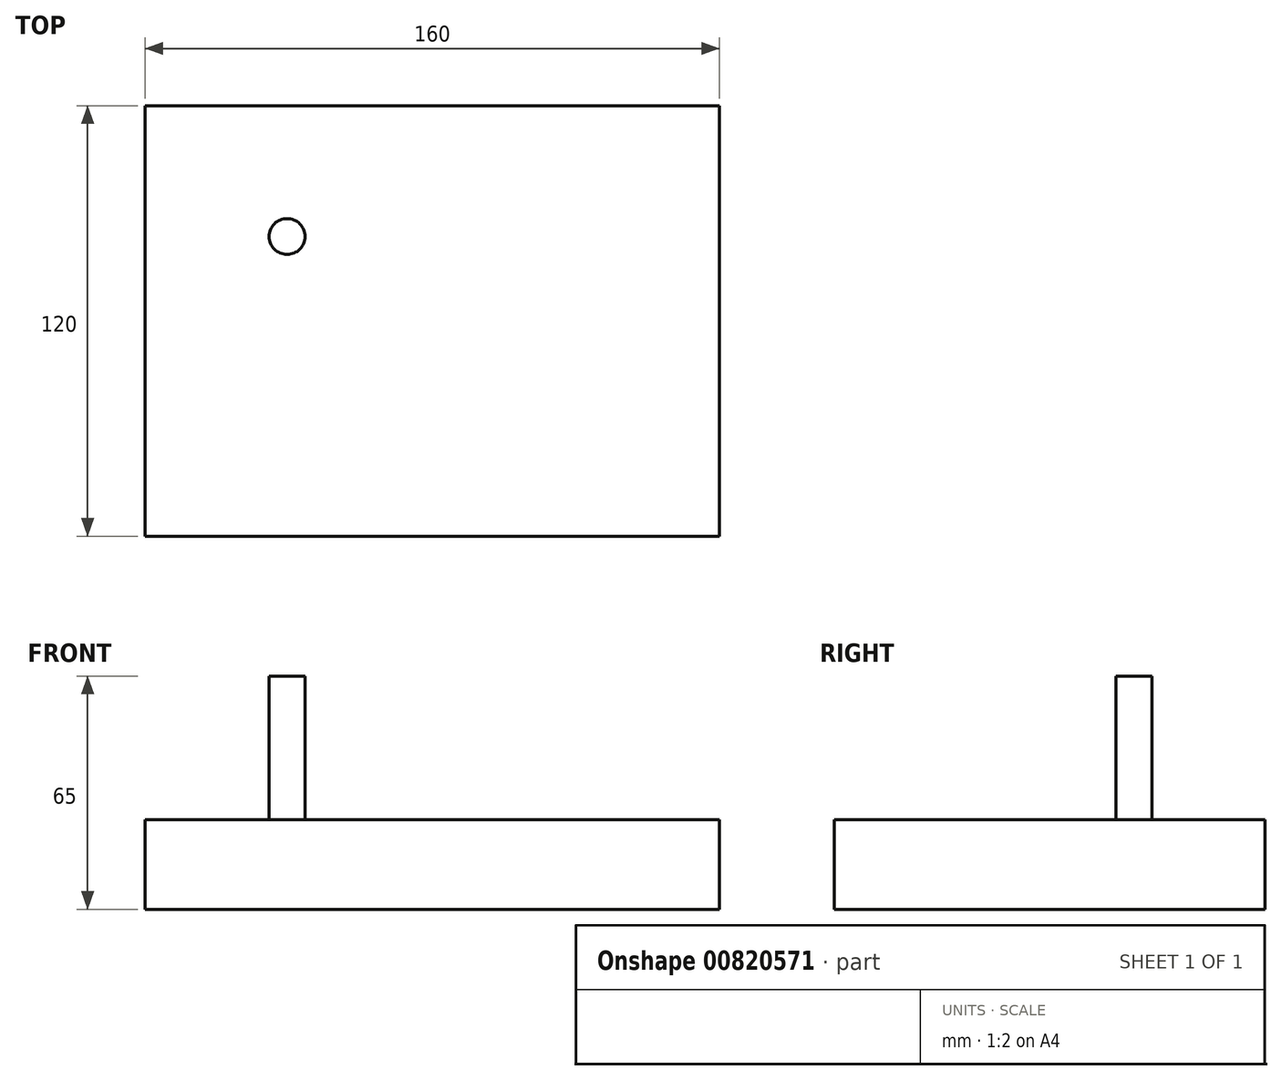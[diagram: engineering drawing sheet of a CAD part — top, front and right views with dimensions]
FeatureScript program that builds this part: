
annotation { "Feature Type Name" : "Feature", "Feature Type Description" : "" }
export const myFeature = defineFeature(function(context is Context, id is Id, definition is map)
    precondition{}
    {
        {
            var Q0;
            Q0=qCreatedBy(makeId("Top.planeOp"),FACE);
            var sketch = newSketch(context, id + "F0", { "sketchPlane" : qUnion([Q0])});
            skLineSegment(sketch, "E0.bottom", {"start": v(-115.2, 57.89) * mm, "end": v(44.8, 57.89) * mm});
            skLineSegment(sketch, "E0.top", {"start": v(-115.2, -62.11) * mm, "end": v(44.8, -62.11) * mm});
            skLineSegment(sketch, "E0.left", {"start": v(-115.2, 57.89) * mm, "end": v(-115.2, -62.11) * mm});
            skLineSegment(sketch, "E0.right", {"start": v(44.8, 57.89) * mm, "end": v(44.8, -62.11) * mm});
            skSolve(sketch);
        }
        {
            var Q0;
            Q0=makeQuery(id+"F0.imprint","IMPRINT",FACE,{"disambiguationData":[TD([[makeQuery(id+"F0.imprint","IMPRINT",EDGE,{"derivedFrom":sQuery(id+"F0.wireOp",EDGE,"E0.bottom")}),-1.0]])]});
            extrude(context, id + "F1", {"entities" : qUnion([Q0]), "depth" : 25 * mm, "offsetDistance" : 25 * mm});
        }
        {
            var Q0;
            Q0=makeQuery(id+"F1.opExtrude","CAP_FACE",FACE,{"disambiguationData":[OSD([sQuery(id+"F0.wireOp",EDGE,"E0.bottom"),sQuery(id+"F0.wireOp",EDGE,"E0.top"),sQuery(id+"F0.wireOp",EDGE,"E0.left"),sQuery(id+"F0.wireOp",EDGE,"E0.right")])],"isStart":false});
            var sketch = newSketch(context, id + "F2", { "sketchPlane" : qUnion([Q0])});
            skPoint(sketch, "E1", {"position": v(-75.65, 21.43) * mm});
            skCircle(sketch, "E2", {"center": v(-75.65, 21.43) * mm, "radius": 5 * mm});
            skSolve(sketch);
        }
        {
            var Q0;
            Q0=makeQuery(id+"F1.opExtrude","CAP_FACE",FACE,{"disambiguationData":[OSD([sQuery(id+"F0.wireOp",EDGE,"E0.bottom"),sQuery(id+"F0.wireOp",EDGE,"E0.top"),sQuery(id+"F0.wireOp",EDGE,"E0.left"),sQuery(id+"F0.wireOp",EDGE,"E0.right")])],"isStart":false});
            var sketch = newSketch(context, id + "F3", { "sketchPlane" : qUnion([Q0])});
            skCircle(sketch, "E3", {"center": v(-35.2, -2.11) * mm, "radius": 5.53 * mm});
            skSolve(sketch);
        }
        {
            var Q0;
            Q0=makeQuery(id+"F2.imprint","IMPRINT",FACE,{"disambiguationData":[TD([[makeQuery(id+"F2.imprint","IMPRINT",EDGE,{"derivedFrom":sQuery(id+"F2.wireOp",EDGE,"E2")}),1.0]])]});
            extrude(context, id + "F4", {"entities" : qUnion([Q0]), "operationType" : NewBodyOperationType.ADD, "depth" : 40 * mm, "offsetDistance" : 25 * mm});
        }
    });
